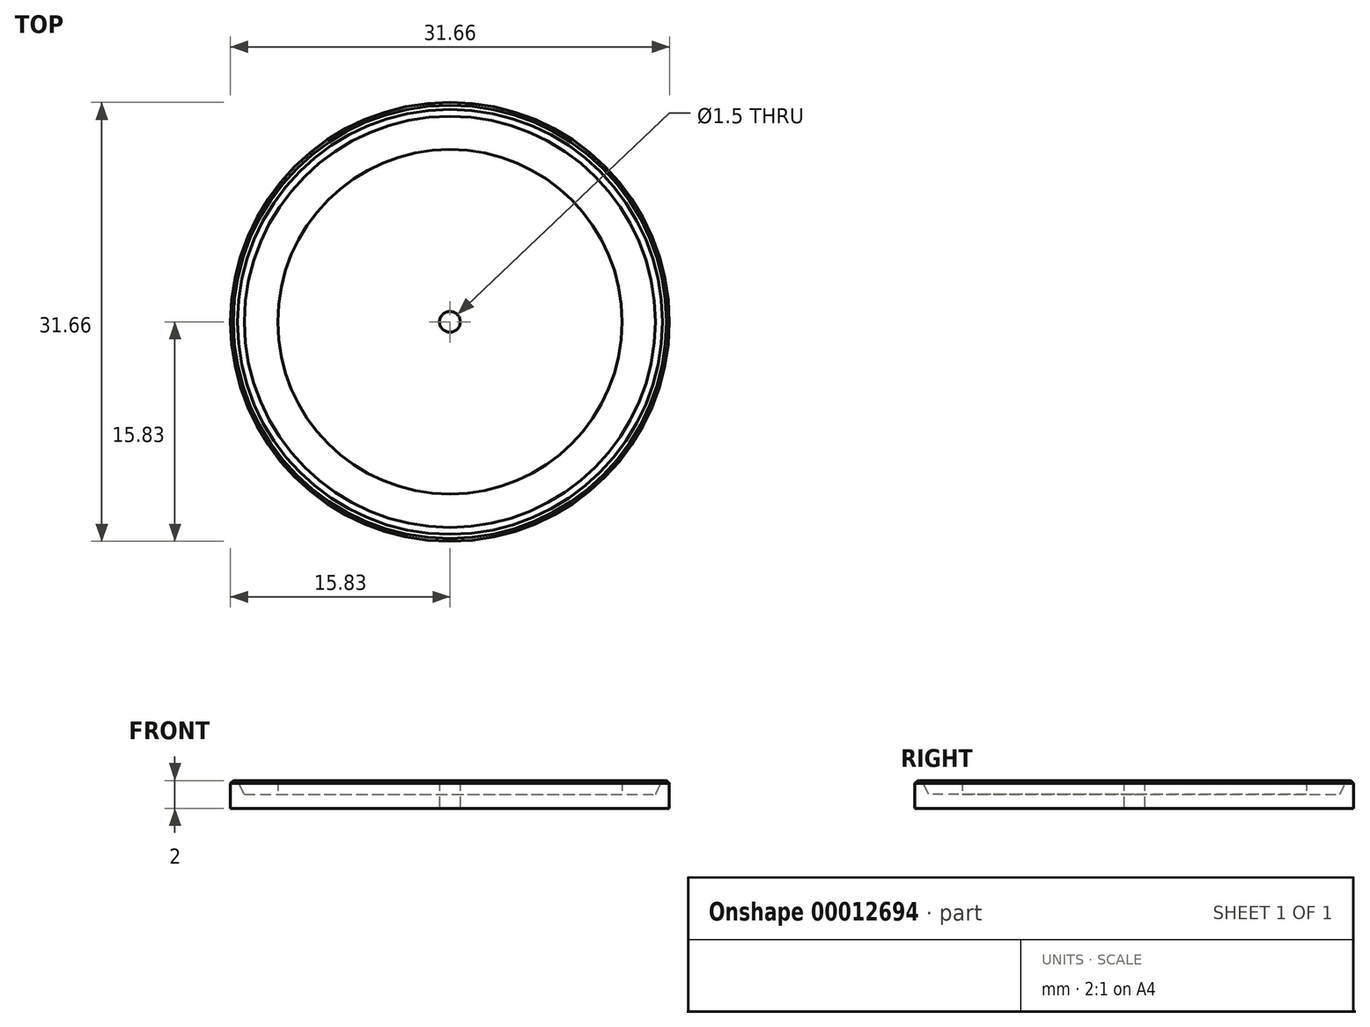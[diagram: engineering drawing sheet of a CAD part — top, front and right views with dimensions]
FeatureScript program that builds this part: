
annotation { "Feature Type Name" : "Feature", "Feature Type Description" : "" }
export const myFeature = defineFeature(function(context is Context, id is Id, definition is map)
    precondition{}
    {
        {
            var Q0;
            Q0=qCreatedBy(makeId("Top.planeOp"),FACE);
            var sketch = newSketch(context, id + "F0", { "sketchPlane" : qUnion([Q0])});
            skCircle(sketch, "E0", {"center": v(0, 0) * mm, "radius": 14.62 * mm, "construction": true});
            skCircle(sketch, "E1", {"center": v(0, 0) * mm, "radius": 14.83 * mm});
            skLineSegment(sketch, "E2", {"start": v(0, 14.62) * mm, "end": v(0, 14.83) * mm, "construction": true});
            skCircle(sketch, "E3", {"center": v(0, 0) * mm, "radius": 15.83 * mm});
            skLineSegment(sketch, "E4", {"start": v(14.4, 3.55) * mm, "end": v(15.37, 3.78) * mm, "construction": true});
            skCircle(sketch, "E5", {"center": v(0, 0) * mm, "radius": 12.63 * mm, "construction": true});
            skLineSegment(sketch, "E6", {"start": v(3.37, 12.17) * mm, "end": v(3.9, 14.1) * mm, "construction": true});
            skCircle(sketch, "E7", {"center": v(0, 0) * mm, "radius": 12.43 * mm});
            skLineSegment(sketch, "E8", {"start": v(0, 12.63) * mm, "end": v(0, 12.43) * mm, "construction": true});
            skCircle(sketch, "E9", {"center": v(0, 0) * mm, "radius": 0.75 * mm});
            skSolve(sketch);
        }
        {
            var Q0;
            Q0 = qSketchRegion(id + "F0", true);
            var Q1;
            Q1=makeQuery(id+"F0.imprint","IMPRINT",FACE,{"disambiguationData":[TD([[makeQuery(id+"F0.imprint","IMPRINT",EDGE,{"derivedFrom":sQuery(id+"F0.wireOp",EDGE,"E7")}),1.0]])]});
            extrude(context, id + "F1", {"entities" : qUnion([Q0, Q1]), "depth" : 2 * mm});
        }
        {
            var Q0;
            Q0=makeQuery(id+"F1.opExtrude","CAP_FACE",FACE,{"disambiguationData":[OSD([sQuery(id+"F0.wireOp",EDGE,"E1"),sQuery(id+"F0.wireOp",EDGE,"E3")])],"isStart":true});
            var sketch = newSketch(context, id + "F2", { "sketchPlane" : qUnion([Q0])});
            skCircle(sketch, "E10.0", {"center": v(0, 0) * mm, "radius": 15.83 * mm});
            skCircle(sketch, "E11.0", {"center": v(0, 0) * mm, "radius": 0.75 * mm});
            skSolve(sketch);
        }
        {
            var Q0;
            Q0 = qSketchRegion(id + "F2", true);
            extrude(context, id + "F3", {"entities" : qUnion([Q0]), "operationType" : NewBodyOperationType.ADD, "oppositeDirection" : true, "depth" : 1 * mm});
        }
        {
            var Q0;
            Q0=makeQuery(id+"F1.opExtrude","CAP_EDGE",EDGE,{"disambiguationData":[OSD([sQuery(id+"F0.wireOp",EDGE,"E3")])],"isStart":false});
            chamfer(context, id + "F4", {"entities" : qUnion([Q0]), "width" : 0.2 * mm, "tangentPropagation" : true});
        }
        {
            var Q0;
            Q0=makeQuery(id+"F1.opExtrude","CAP_EDGE",EDGE,{"disambiguationData":[OSD([sQuery(id+"F0.wireOp",EDGE,"E1")])],"isStart":false});
            chamfer(context, id + "F5", {"entities" : qUnion([Q0]), "chamferType" : ChamferType.TWO_OFFSETS, "width1" : 1 * mm, "oppositeDirection" : false, "width2" : 0.5 * mm, "tangentPropagation" : true});
        }
    });
